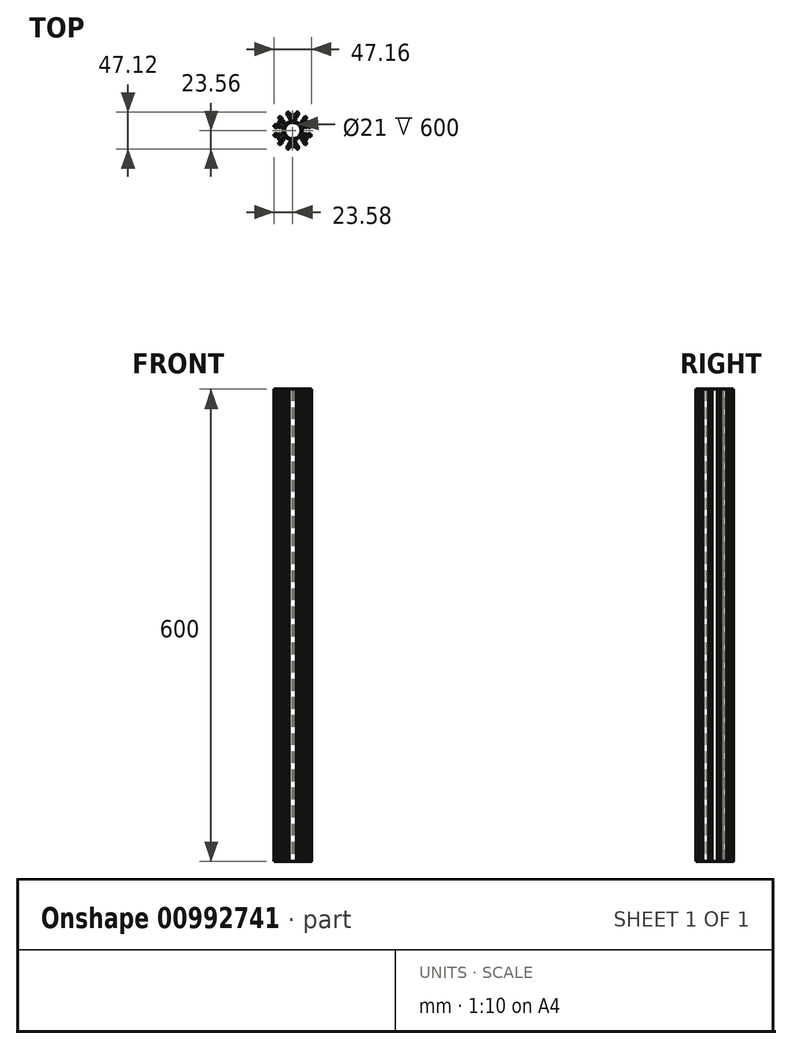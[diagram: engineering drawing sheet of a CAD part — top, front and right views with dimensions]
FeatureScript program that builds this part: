
annotation { "Feature Type Name" : "Feature", "Feature Type Description" : "" }
export const myFeature = defineFeature(function(context is Context, id is Id, definition is map)
    precondition{}
    {
        {
            var Q0;
            Q0=qCreatedBy(makeId("Top.planeOp"),FACE);
            var sketch = newSketch(context, id + "F0", { "sketchPlane" : qUnion([Q0])});
            skLineSegment(sketch, "E0.bottom", {"start": v(-7.45, -23.56) * mm, "end": v(-4.75, -23.56) * mm});
            skLineSegment(sketch, "E0.top", {"start": v(-7.45, -19.16) * mm, "end": v(-1, -19.16) * mm});
            skLineSegment(sketch, "E0.left", {"start": v(-7.45, -23.56) * mm, "end": v(-7.45, -19.16) * mm});
            skLineSegment(sketch, "E0.right", {"start": v(7.45, -23.56) * mm, "end": v(7.45, -19.16) * mm});
            skLineSegment(sketch, "E1.bottom", {"start": v(-6.25, -22.36) * mm, "end": v(-4.75, -22.36) * mm});
            skLineSegment(sketch, "E1.top", {"start": v(-6.25, -20.36) * mm, "end": v(6.25, -20.36) * mm});
            skLineSegment(sketch, "E1.left", {"start": v(-6.25, -22.36) * mm, "end": v(-6.25, -20.36) * mm});
            skLineSegment(sketch, "E1.right", {"start": v(6.25, -22.36) * mm, "end": v(6.25, -20.36) * mm});
            skLineSegment(sketch, "E2.left", {"start": v(-1, -19.16) * mm, "end": v(-1, -17.46) * mm});
            skLineSegment(sketch, "E2.right", {"start": v(1, -19.16) * mm, "end": v(1, -17.46) * mm});
            skArc(sketch, "E3", {"start": v(1, -12.46) * mm, "mid": v(6.25, -10.83) * mm, "end": v(10.3, -7.1) * mm});
            skLineSegment(sketch, "E4.left", {"start": v(-4.75, -23.56) * mm, "end": v(-4.75, -22.36) * mm});
            skLineSegment(sketch, "E4.right", {"start": v(4.75, -23.56) * mm, "end": v(4.75, -22.36) * mm});
            skLineSegment(sketch, "E5.trimOffspring", {"start": v(4.75, -23.56) * mm, "end": v(7.45, -23.56) * mm});
            skLineSegment(sketch, "E6.trimOffspring", {"start": v(4.75, -22.36) * mm, "end": v(6.25, -22.36) * mm});
            skLineSegment(sketch, "E7.trimOffspring", {"start": v(1, -19.16) * mm, "end": v(7.45, -19.16) * mm});
            skCircle(sketch, "E8", {"center": v(0, 0) * mm, "radius": 10.5 * mm});
            skLineSegment(sketch, "E9.bottom", {"start": v(-5.5, -17.46) * mm, "end": v(-1, -17.46) * mm});
            skLineSegment(sketch, "E9.top", {"start": v(-5.5, -16.46) * mm, "end": v(-1, -16.46) * mm});
            skLineSegment(sketch, "E9.left", {"start": v(-5.5, -17.46) * mm, "end": v(-5.5, -16.46) * mm});
            skLineSegment(sketch, "E9.right", {"start": v(5.5, -17.46) * mm, "end": v(5.5, -16.46) * mm});
            skLineSegment(sketch, "E10.bottom", {"start": v(-4, -14.86) * mm, "end": v(-1, -14.86) * mm});
            skLineSegment(sketch, "E10.top", {"start": v(-4, -13.86) * mm, "end": v(-1, -13.86) * mm});
            skLineSegment(sketch, "E10.left", {"start": v(-4, -14.86) * mm, "end": v(-4, -13.86) * mm});
            skLineSegment(sketch, "E10.right", {"start": v(4, -14.86) * mm, "end": v(4, -13.86) * mm});
            skLineSegment(sketch, "E11.trimOffspring", {"start": v(1, -17.46) * mm, "end": v(5.5, -17.46) * mm});
            skLineSegment(sketch, "E12.trimOffspring", {"start": v(-1, -16.46) * mm, "end": v(-1, -14.86) * mm});
            skLineSegment(sketch, "E13.trimOffspring", {"start": v(1, -16.46) * mm, "end": v(5.5, -16.46) * mm});
            skLineSegment(sketch, "E14.trimOffspring", {"start": v(1, -14.86) * mm, "end": v(4, -14.86) * mm});
            skLineSegment(sketch, "E15.trimOffspring", {"start": v(1, -16.46) * mm, "end": v(1, -14.86) * mm});
            skLineSegment(sketch, "E16.trimOffspring", {"start": v(1, -13.86) * mm, "end": v(1, -12.46) * mm});
            skLineSegment(sketch, "E17.trimOffspring", {"start": v(-1, -13.86) * mm, "end": v(-1, -12.46) * mm});
            skLineSegment(sketch, "E18.trimOffspring", {"start": v(1, -13.86) * mm, "end": v(4, -13.86) * mm});
            skLineSegment(sketch, "E19.1.0", {"start": v(16.68, -18.23) * mm, "end": v(18.03, -15.9) * mm});
            skLineSegment(sketch, "E19.1.1", {"start": v(13.37, -6.56) * mm, "end": v(14.87, -3.97) * mm});
            skLineSegment(sketch, "E19.1.2", {"start": v(12.87, -16.03) * mm, "end": v(16.1, -10.45) * mm});
            skLineSegment(sketch, "E19.1.3", {"start": v(24.13, -5.33) * mm, "end": v(20.32, -3.13) * mm});
            skLineSegment(sketch, "E19.1.4", {"start": v(10.87, -10.9) * mm, "end": v(12.37, -8.3) * mm});
            skLineSegment(sketch, "E19.1.5", {"start": v(10, -10.4) * mm, "end": v(11.5, -7.8) * mm});
            skLineSegment(sketch, "E19.1.6", {"start": v(16.24, -16.6) * mm, "end": v(14.5, -15.6) * mm});
            skLineSegment(sketch, "E19.1.7", {"start": v(14.75, -7.36) * mm, "end": v(17, -3.47) * mm});
            skLineSegment(sketch, "E19.1.8", {"start": v(12.5, -6.06) * mm, "end": v(14, -3.47) * mm});
            skLineSegment(sketch, "E19.1.9", {"start": v(22.78, -7.67) * mm, "end": v(24.13, -5.33) * mm});
            skLineSegment(sketch, "E19.1.10", {"start": v(14.5, -15.6) * mm, "end": v(20.76, -4.77) * mm});
            skLineSegment(sketch, "E19.1.11", {"start": v(22.49, -5.77) * mm, "end": v(20.76, -4.77) * mm});
            skLineSegment(sketch, "E19.1.12", {"start": v(16.68, -18.23) * mm, "end": v(12.87, -16.03) * mm});
            skLineSegment(sketch, "E19.1.13", {"start": v(17.1, -8.71) * mm, "end": v(20.32, -3.13) * mm});
            skLineSegment(sketch, "E19.1.14", {"start": v(12.37, -13.5) * mm, "end": v(14.62, -9.6) * mm});
            skLineSegment(sketch, "E19.1.15", {"start": v(11.5, -13) * mm, "end": v(13.75, -9.1) * mm});
            skLineSegment(sketch, "E19.1.16", {"start": v(15.62, -7.86) * mm, "end": v(17.87, -3.97) * mm});
            skLineSegment(sketch, "E19.1.17", {"start": v(22.78, -7.67) * mm, "end": v(21.74, -7.07) * mm});
            skLineSegment(sketch, "E19.1.18", {"start": v(13.75, -9.1) * mm, "end": v(12.37, -8.3) * mm});
            skLineSegment(sketch, "E19.1.19", {"start": v(14.87, -3.97) * mm, "end": v(14, -3.47) * mm});
            skLineSegment(sketch, "E19.1.20", {"start": v(21.74, -7.07) * mm, "end": v(22.49, -5.77) * mm});
            skLineSegment(sketch, "E19.1.21", {"start": v(18.03, -15.9) * mm, "end": v(16.99, -15.3) * mm});
            skLineSegment(sketch, "E19.1.22", {"start": v(10.87, -10.9) * mm, "end": v(10, -10.4) * mm});
            skLineSegment(sketch, "E19.1.23", {"start": v(12.37, -13.5) * mm, "end": v(11.5, -13) * mm});
            skLineSegment(sketch, "E19.1.24", {"start": v(16.1, -10.45) * mm, "end": v(14.62, -9.6) * mm});
            skLineSegment(sketch, "E19.1.25", {"start": v(17.1, -8.71) * mm, "end": v(15.62, -7.86) * mm});
            skLineSegment(sketch, "E19.1.26", {"start": v(16.24, -16.6) * mm, "end": v(16.99, -15.3) * mm});
            skLineSegment(sketch, "E19.1.27", {"start": v(17.87, -3.97) * mm, "end": v(17, -3.47) * mm});
            skLineSegment(sketch, "E19.1.28", {"start": v(14.75, -7.36) * mm, "end": v(13.37, -6.56) * mm});
            skLineSegment(sketch, "E19.1.29", {"start": v(11.5, -7.8) * mm, "end": v(10.3, -7.1) * mm});
            skLineSegment(sketch, "E19.1.30", {"start": v(12.5, -6.06) * mm, "end": v(11.3, -5.36) * mm});
            skLineSegment(sketch, "E19.2.0", {"start": v(24.13, 5.33) * mm, "end": v(22.78, 7.67) * mm});
            skLineSegment(sketch, "E19.2.1", {"start": v(12.37, 8.3) * mm, "end": v(10.87, 10.9) * mm});
            skLineSegment(sketch, "E19.2.2", {"start": v(20.32, 3.13) * mm, "end": v(17.1, 8.71) * mm});
            skLineSegment(sketch, "E19.2.3", {"start": v(16.68, 18.23) * mm, "end": v(12.87, 16.03) * mm});
            skLineSegment(sketch, "E19.2.4", {"start": v(14.87, 3.97) * mm, "end": v(13.37, 6.56) * mm});
            skLineSegment(sketch, "E19.2.5", {"start": v(14, 3.47) * mm, "end": v(12.5, 6.06) * mm});
            skLineSegment(sketch, "E19.2.6", {"start": v(22.49, 5.77) * mm, "end": v(20.76, 4.77) * mm});
            skLineSegment(sketch, "E19.2.7", {"start": v(13.75, 9.1) * mm, "end": v(11.5, 13) * mm});
            skLineSegment(sketch, "E19.2.8", {"start": v(11.5, 7.8) * mm, "end": v(10, 10.4) * mm});
            skLineSegment(sketch, "E19.2.9", {"start": v(18.03, 15.9) * mm, "end": v(16.68, 18.23) * mm});
            skLineSegment(sketch, "E19.2.10", {"start": v(20.76, 4.77) * mm, "end": v(14.5, 15.6) * mm});
            skLineSegment(sketch, "E19.2.11", {"start": v(16.24, 16.6) * mm, "end": v(14.5, 15.6) * mm});
            skLineSegment(sketch, "E19.2.12", {"start": v(24.13, 5.33) * mm, "end": v(20.32, 3.13) * mm});
            skLineSegment(sketch, "E19.2.13", {"start": v(16.1, 10.45) * mm, "end": v(12.87, 16.03) * mm});
            skLineSegment(sketch, "E19.2.14", {"start": v(17.87, 3.97) * mm, "end": v(15.62, 7.86) * mm});
            skLineSegment(sketch, "E19.2.15", {"start": v(17, 3.47) * mm, "end": v(14.75, 7.36) * mm});
            skLineSegment(sketch, "E19.2.16", {"start": v(14.62, 9.6) * mm, "end": v(12.37, 13.5) * mm});
            skLineSegment(sketch, "E19.2.17", {"start": v(18.03, 15.9) * mm, "end": v(16.99, 15.3) * mm});
            skLineSegment(sketch, "E19.2.18", {"start": v(14.75, 7.36) * mm, "end": v(13.37, 6.56) * mm});
            skLineSegment(sketch, "E19.2.19", {"start": v(10.87, 10.9) * mm, "end": v(10, 10.4) * mm});
            skLineSegment(sketch, "E19.2.20", {"start": v(16.99, 15.3) * mm, "end": v(16.24, 16.6) * mm});
            skLineSegment(sketch, "E19.2.21", {"start": v(22.78, 7.67) * mm, "end": v(21.74, 7.07) * mm});
            skLineSegment(sketch, "E19.2.22", {"start": v(14.87, 3.97) * mm, "end": v(14, 3.47) * mm});
            skLineSegment(sketch, "E19.2.23", {"start": v(17.87, 3.97) * mm, "end": v(17, 3.47) * mm});
            skLineSegment(sketch, "E19.2.24", {"start": v(17.1, 8.71) * mm, "end": v(15.62, 7.86) * mm});
            skLineSegment(sketch, "E19.2.25", {"start": v(16.1, 10.45) * mm, "end": v(14.62, 9.6) * mm});
            skLineSegment(sketch, "E19.2.26", {"start": v(22.49, 5.77) * mm, "end": v(21.74, 7.07) * mm});
            skLineSegment(sketch, "E19.2.27", {"start": v(12.37, 13.5) * mm, "end": v(11.5, 13) * mm});
            skLineSegment(sketch, "E19.2.28", {"start": v(13.75, 9.1) * mm, "end": v(12.37, 8.3) * mm});
            skLineSegment(sketch, "E19.2.29", {"start": v(12.5, 6.06) * mm, "end": v(11.3, 5.36) * mm});
            skLineSegment(sketch, "E19.2.30", {"start": v(11.5, 7.8) * mm, "end": v(10.3, 7.1) * mm});
            skLineSegment(sketch, "E19.3.0", {"start": v(7.45, 23.56) * mm, "end": v(4.75, 23.56) * mm});
            skLineSegment(sketch, "E19.3.1", {"start": v(-1, 14.86) * mm, "end": v(-4, 14.86) * mm});
            skLineSegment(sketch, "E19.3.2", {"start": v(7.45, 19.16) * mm, "end": v(1, 19.16) * mm});
            skLineSegment(sketch, "E19.3.3", {"start": v(-7.45, 23.56) * mm, "end": v(-7.45, 19.16) * mm});
            skLineSegment(sketch, "E19.3.4", {"start": v(4, 14.86) * mm, "end": v(1, 14.86) * mm});
            skLineSegment(sketch, "E19.3.5", {"start": v(4, 13.86) * mm, "end": v(1, 13.86) * mm});
            skLineSegment(sketch, "E19.3.6", {"start": v(6.25, 22.36) * mm, "end": v(6.25, 20.36) * mm});
            skLineSegment(sketch, "E19.3.7", {"start": v(-1, 16.46) * mm, "end": v(-5.5, 16.46) * mm});
            skLineSegment(sketch, "E19.3.8", {"start": v(-1, 13.86) * mm, "end": v(-4, 13.86) * mm});
            skLineSegment(sketch, "E19.3.9", {"start": v(-4.75, 23.56) * mm, "end": v(-7.45, 23.56) * mm});
            skLineSegment(sketch, "E19.3.10", {"start": v(6.25, 20.36) * mm, "end": v(-6.25, 20.36) * mm});
            skLineSegment(sketch, "E19.3.11", {"start": v(-6.25, 22.36) * mm, "end": v(-6.25, 20.36) * mm});
            skLineSegment(sketch, "E19.3.12", {"start": v(7.45, 23.56) * mm, "end": v(7.45, 19.16) * mm});
            skLineSegment(sketch, "E19.3.13", {"start": v(-1, 19.16) * mm, "end": v(-7.45, 19.16) * mm});
            skLineSegment(sketch, "E19.3.14", {"start": v(5.5, 17.46) * mm, "end": v(1, 17.46) * mm});
            skLineSegment(sketch, "E19.3.15", {"start": v(5.5, 16.46) * mm, "end": v(1, 16.46) * mm});
            skLineSegment(sketch, "E19.3.16", {"start": v(-1, 17.46) * mm, "end": v(-5.5, 17.46) * mm});
            skLineSegment(sketch, "E19.3.17", {"start": v(-4.75, 23.56) * mm, "end": v(-4.75, 22.36) * mm});
            skLineSegment(sketch, "E19.3.18", {"start": v(1, 16.46) * mm, "end": v(1, 14.86) * mm});
            skLineSegment(sketch, "E19.3.19", {"start": v(-4, 14.86) * mm, "end": v(-4, 13.86) * mm});
            skLineSegment(sketch, "E19.3.20", {"start": v(-4.75, 22.36) * mm, "end": v(-6.25, 22.36) * mm});
            skLineSegment(sketch, "E19.3.21", {"start": v(4.75, 23.56) * mm, "end": v(4.75, 22.36) * mm});
            skLineSegment(sketch, "E19.3.22", {"start": v(4, 14.86) * mm, "end": v(4, 13.86) * mm});
            skLineSegment(sketch, "E19.3.23", {"start": v(5.5, 17.46) * mm, "end": v(5.5, 16.46) * mm});
            skLineSegment(sketch, "E19.3.24", {"start": v(1, 19.16) * mm, "end": v(1, 17.46) * mm});
            skLineSegment(sketch, "E19.3.25", {"start": v(-1, 19.16) * mm, "end": v(-1, 17.46) * mm});
            skLineSegment(sketch, "E19.3.26", {"start": v(6.25, 22.36) * mm, "end": v(4.75, 22.36) * mm});
            skLineSegment(sketch, "E19.3.27", {"start": v(-5.5, 17.46) * mm, "end": v(-5.5, 16.46) * mm});
            skLineSegment(sketch, "E19.3.28", {"start": v(-1, 16.46) * mm, "end": v(-1, 14.86) * mm});
            skLineSegment(sketch, "E19.3.29", {"start": v(1, 13.86) * mm, "end": v(1, 12.46) * mm});
            skLineSegment(sketch, "E19.3.30", {"start": v(-1, 13.86) * mm, "end": v(-1, 12.46) * mm});
            skLineSegment(sketch, "E19.4.0", {"start": v(-16.68, 18.23) * mm, "end": v(-18.03, 15.9) * mm});
            skLineSegment(sketch, "E19.4.1", {"start": v(-13.37, 6.56) * mm, "end": v(-14.87, 3.97) * mm});
            skLineSegment(sketch, "E19.4.2", {"start": v(-12.87, 16.03) * mm, "end": v(-16.1, 10.45) * mm});
            skLineSegment(sketch, "E19.4.3", {"start": v(-24.13, 5.33) * mm, "end": v(-20.32, 3.13) * mm});
            skLineSegment(sketch, "E19.4.4", {"start": v(-10.87, 10.9) * mm, "end": v(-12.37, 8.3) * mm});
            skLineSegment(sketch, "E19.4.5", {"start": v(-10, 10.4) * mm, "end": v(-11.5, 7.8) * mm});
            skLineSegment(sketch, "E19.4.6", {"start": v(-16.24, 16.6) * mm, "end": v(-14.5, 15.6) * mm});
            skLineSegment(sketch, "E19.4.7", {"start": v(-14.75, 7.36) * mm, "end": v(-17, 3.47) * mm});
            skLineSegment(sketch, "E19.4.8", {"start": v(-12.5, 6.06) * mm, "end": v(-14, 3.47) * mm});
            skLineSegment(sketch, "E19.4.9", {"start": v(-22.78, 7.67) * mm, "end": v(-24.13, 5.33) * mm});
            skLineSegment(sketch, "E19.4.10", {"start": v(-14.5, 15.6) * mm, "end": v(-20.76, 4.77) * mm});
            skLineSegment(sketch, "E19.4.11", {"start": v(-22.49, 5.77) * mm, "end": v(-20.76, 4.77) * mm});
            skLineSegment(sketch, "E19.4.12", {"start": v(-16.68, 18.23) * mm, "end": v(-12.87, 16.03) * mm});
            skLineSegment(sketch, "E19.4.13", {"start": v(-17.1, 8.71) * mm, "end": v(-20.32, 3.13) * mm});
            skLineSegment(sketch, "E19.4.14", {"start": v(-12.37, 13.5) * mm, "end": v(-14.62, 9.6) * mm});
            skLineSegment(sketch, "E19.4.15", {"start": v(-11.5, 13) * mm, "end": v(-13.75, 9.1) * mm});
            skLineSegment(sketch, "E19.4.16", {"start": v(-15.62, 7.86) * mm, "end": v(-17.87, 3.97) * mm});
            skLineSegment(sketch, "E19.4.17", {"start": v(-22.78, 7.67) * mm, "end": v(-21.74, 7.07) * mm});
            skLineSegment(sketch, "E19.4.18", {"start": v(-13.75, 9.1) * mm, "end": v(-12.37, 8.3) * mm});
            skLineSegment(sketch, "E19.4.19", {"start": v(-14.87, 3.97) * mm, "end": v(-14, 3.47) * mm});
            skLineSegment(sketch, "E19.4.20", {"start": v(-21.74, 7.07) * mm, "end": v(-22.49, 5.77) * mm});
            skLineSegment(sketch, "E19.4.21", {"start": v(-18.03, 15.9) * mm, "end": v(-16.99, 15.3) * mm});
            skLineSegment(sketch, "E19.4.22", {"start": v(-10.87, 10.9) * mm, "end": v(-10, 10.4) * mm});
            skLineSegment(sketch, "E19.4.23", {"start": v(-12.37, 13.5) * mm, "end": v(-11.5, 13) * mm});
            skLineSegment(sketch, "E19.4.24", {"start": v(-16.1, 10.45) * mm, "end": v(-14.62, 9.6) * mm});
            skLineSegment(sketch, "E19.4.25", {"start": v(-17.1, 8.71) * mm, "end": v(-15.62, 7.86) * mm});
            skLineSegment(sketch, "E19.4.26", {"start": v(-16.24, 16.6) * mm, "end": v(-16.99, 15.3) * mm});
            skLineSegment(sketch, "E19.4.27", {"start": v(-17.87, 3.97) * mm, "end": v(-17, 3.47) * mm});
            skLineSegment(sketch, "E19.4.28", {"start": v(-14.75, 7.36) * mm, "end": v(-13.37, 6.56) * mm});
            skLineSegment(sketch, "E19.4.29", {"start": v(-11.5, 7.8) * mm, "end": v(-10.3, 7.1) * mm});
            skLineSegment(sketch, "E19.4.30", {"start": v(-12.5, 6.06) * mm, "end": v(-11.3, 5.36) * mm});
            skLineSegment(sketch, "E19.5.0", {"start": v(-24.13, -5.33) * mm, "end": v(-22.78, -7.67) * mm});
            skLineSegment(sketch, "E19.5.1", {"start": v(-12.37, -8.3) * mm, "end": v(-10.87, -10.9) * mm});
            skLineSegment(sketch, "E19.5.2", {"start": v(-20.32, -3.13) * mm, "end": v(-17.1, -8.71) * mm});
            skLineSegment(sketch, "E19.5.3", {"start": v(-16.68, -18.23) * mm, "end": v(-12.87, -16.03) * mm});
            skLineSegment(sketch, "E19.5.4", {"start": v(-14.87, -3.97) * mm, "end": v(-13.37, -6.56) * mm});
            skLineSegment(sketch, "E19.5.5", {"start": v(-14, -3.47) * mm, "end": v(-12.5, -6.06) * mm});
            skLineSegment(sketch, "E19.5.6", {"start": v(-22.49, -5.77) * mm, "end": v(-20.76, -4.77) * mm});
            skLineSegment(sketch, "E19.5.7", {"start": v(-13.75, -9.1) * mm, "end": v(-11.5, -13) * mm});
            skLineSegment(sketch, "E19.5.8", {"start": v(-11.5, -7.8) * mm, "end": v(-10, -10.4) * mm});
            skLineSegment(sketch, "E19.5.9", {"start": v(-18.03, -15.9) * mm, "end": v(-16.68, -18.23) * mm});
            skLineSegment(sketch, "E19.5.10", {"start": v(-20.76, -4.77) * mm, "end": v(-14.5, -15.6) * mm});
            skLineSegment(sketch, "E19.5.11", {"start": v(-16.24, -16.6) * mm, "end": v(-14.5, -15.6) * mm});
            skLineSegment(sketch, "E19.5.12", {"start": v(-24.13, -5.33) * mm, "end": v(-20.32, -3.13) * mm});
            skLineSegment(sketch, "E19.5.13", {"start": v(-16.1, -10.45) * mm, "end": v(-12.87, -16.03) * mm});
            skLineSegment(sketch, "E19.5.14", {"start": v(-17.87, -3.97) * mm, "end": v(-15.62, -7.86) * mm});
            skLineSegment(sketch, "E19.5.15", {"start": v(-17, -3.47) * mm, "end": v(-14.75, -7.36) * mm});
            skLineSegment(sketch, "E19.5.16", {"start": v(-14.62, -9.6) * mm, "end": v(-12.37, -13.5) * mm});
            skLineSegment(sketch, "E19.5.17", {"start": v(-18.03, -15.9) * mm, "end": v(-16.99, -15.3) * mm});
            skLineSegment(sketch, "E19.5.18", {"start": v(-14.75, -7.36) * mm, "end": v(-13.37, -6.56) * mm});
            skLineSegment(sketch, "E19.5.19", {"start": v(-10.87, -10.9) * mm, "end": v(-10, -10.4) * mm});
            skLineSegment(sketch, "E19.5.20", {"start": v(-16.99, -15.3) * mm, "end": v(-16.24, -16.6) * mm});
            skLineSegment(sketch, "E19.5.21", {"start": v(-22.78, -7.67) * mm, "end": v(-21.74, -7.07) * mm});
            skLineSegment(sketch, "E19.5.22", {"start": v(-14.87, -3.97) * mm, "end": v(-14, -3.47) * mm});
            skLineSegment(sketch, "E19.5.23", {"start": v(-17.87, -3.97) * mm, "end": v(-17, -3.47) * mm});
            skLineSegment(sketch, "E19.5.24", {"start": v(-17.1, -8.71) * mm, "end": v(-15.62, -7.86) * mm});
            skLineSegment(sketch, "E19.5.25", {"start": v(-16.1, -10.45) * mm, "end": v(-14.62, -9.6) * mm});
            skLineSegment(sketch, "E19.5.26", {"start": v(-22.49, -5.77) * mm, "end": v(-21.74, -7.07) * mm});
            skLineSegment(sketch, "E19.5.27", {"start": v(-12.37, -13.5) * mm, "end": v(-11.5, -13) * mm});
            skLineSegment(sketch, "E19.5.28", {"start": v(-13.75, -9.1) * mm, "end": v(-12.37, -8.3) * mm});
            skLineSegment(sketch, "E19.5.29", {"start": v(-12.5, -6.06) * mm, "end": v(-11.3, -5.36) * mm});
            skLineSegment(sketch, "E19.5.30", {"start": v(-11.5, -7.8) * mm, "end": v(-10.3, -7.1) * mm});
            skArc(sketch, "E20.trimOffspring", {"start": v(-10.3, -7.1) * mm, "mid": v(-6.25, -10.83) * mm, "end": v(-1, -12.46) * mm});
            skArc(sketch, "E21.trimOffspring", {"start": v(-11.3, 5.36) * mm, "mid": v(-12.5, 0) * mm, "end": v(-11.3, -5.36) * mm});
            skArc(sketch, "E22.trimOffspring", {"start": v(11.3, -5.36) * mm, "mid": v(12.5, 0) * mm, "end": v(11.3, 5.36) * mm});
            skArc(sketch, "E23.trimOffspring", {"start": v(-1, 12.46) * mm, "mid": v(-6.25, 10.83) * mm, "end": v(-10.3, 7.1) * mm});
            skArc(sketch, "E24.trimOffspring", {"start": v(10.3, 7.1) * mm, "mid": v(6.25, 10.83) * mm, "end": v(1, 12.46) * mm});
            skSolve(sketch);
        }
        {
            var Q0;
            Q0=qSketchRegion(id+"F0",true);
            extrude(context, id + "F1", {"entities" : qUnion([Q0]), "depth" : 600 * mm, "offsetDistance" : 25 * mm});
        }
        {
            var Q0;
            Q0=makeQuery(id+"F1.opExtrude","SWEPT_EDGE",EDGE,{"disambiguationData":[OSD([sQuery(id+"F0.wireOp",EDGE,"E19.3.2"),sQuery(id+"F0.wireOp",EDGE,"E19.3.12")])]});
            var Q1;
            Q1=makeQuery(id+"F1.opExtrude","SWEPT_EDGE",EDGE,{"disambiguationData":[OSD([sQuery(id+"F0.wireOp",EDGE,"E19.3.3"),sQuery(id+"F0.wireOp",EDGE,"E19.3.13")])]});
            var Q2;
            Q2=makeQuery(id+"F1.opExtrude","SWEPT_EDGE",EDGE,{"disambiguationData":[OSD([sQuery(id+"F0.wireOp",EDGE,"E19.2.3"),sQuery(id+"F0.wireOp",EDGE,"E19.2.13")])]});
            var Q3;
            Q3=makeQuery(id+"F1.opExtrude","SWEPT_EDGE",EDGE,{"disambiguationData":[OSD([sQuery(id+"F0.wireOp",EDGE,"E19.2.2"),sQuery(id+"F0.wireOp",EDGE,"E19.2.12")])]});
            var Q4;
            Q4=makeQuery(id+"F1.opExtrude","SWEPT_EDGE",EDGE,{"disambiguationData":[OSD([sQuery(id+"F0.wireOp",EDGE,"E19.1.3"),sQuery(id+"F0.wireOp",EDGE,"E19.1.13")])]});
            var Q5;
            Q5=makeQuery(id+"F1.opExtrude","SWEPT_EDGE",EDGE,{"disambiguationData":[OSD([sQuery(id+"F0.wireOp",EDGE,"E19.1.2"),sQuery(id+"F0.wireOp",EDGE,"E19.1.12")])]});
            var Q6;
            Q6=makeQuery(id+"F1.opExtrude","SWEPT_EDGE",EDGE,{"disambiguationData":[OSD([sQuery(id+"F0.wireOp",EDGE,"E0.right"),sQuery(id+"F0.wireOp",EDGE,"E7.trimOffspring")])]});
            var Q7;
            Q7=makeQuery(id+"F1.opExtrude","SWEPT_EDGE",EDGE,{"disambiguationData":[OSD([sQuery(id+"F0.wireOp",EDGE,"E0.top"),sQuery(id+"F0.wireOp",EDGE,"E0.left")])]});
            var Q8;
            Q8=makeQuery(id+"F1.opExtrude","SWEPT_EDGE",EDGE,{"disambiguationData":[OSD([sQuery(id+"F0.wireOp",EDGE,"E19.5.3"),sQuery(id+"F0.wireOp",EDGE,"E19.5.13")])]});
            var Q9;
            Q9=makeQuery(id+"F1.opExtrude","SWEPT_EDGE",EDGE,{"disambiguationData":[OSD([sQuery(id+"F0.wireOp",EDGE,"E19.5.2"),sQuery(id+"F0.wireOp",EDGE,"E19.5.12")])]});
            var Q10;
            Q10=makeQuery(id+"F1.opExtrude","SWEPT_EDGE",EDGE,{"disambiguationData":[OSD([sQuery(id+"F0.wireOp",EDGE,"E19.4.3"),sQuery(id+"F0.wireOp",EDGE,"E19.4.13")])]});
            var Q11;
            Q11=makeQuery(id+"F1.opExtrude","SWEPT_EDGE",EDGE,{"disambiguationData":[OSD([sQuery(id+"F0.wireOp",EDGE,"E19.4.2"),sQuery(id+"F0.wireOp",EDGE,"E19.4.12")])]});
            fillet(context, id + "F2", {"entities" : qUnion([Q0, Q1, Q2, Q3, Q4, Q5, Q6, Q7, Q8, Q9, Q10, Q11]), "tangentPropagation" : true, "radius" : 1.5 * mm, "defaultsChanged" : true, "vertexSettings" : [], "allowEdgeOverflow" : false});
        }
        {
            var Q0;
            Q0=makeQuery(id+"F1.opExtrude","SWEPT_EDGE",EDGE,{"disambiguationData":[OSD([sQuery(id+"F0.wireOp",EDGE,"E19.3.0"),sQuery(id+"F0.wireOp",EDGE,"E19.3.21")])]});
            var Q1;
            Q1=makeQuery(id+"F1.opExtrude","SWEPT_EDGE",EDGE,{"disambiguationData":[OSD([sQuery(id+"F0.wireOp",EDGE,"E19.3.9"),sQuery(id+"F0.wireOp",EDGE,"E19.3.17")])]});
            var Q2;
            Q2=makeQuery(id+"F1.opExtrude","SWEPT_EDGE",EDGE,{"disambiguationData":[OSD([sQuery(id+"F0.wireOp",EDGE,"E19.3.16"),sQuery(id+"F0.wireOp",EDGE,"E19.3.27")])]});
            var Q3;
            Q3=makeQuery(id+"F1.opExtrude","SWEPT_EDGE",EDGE,{"disambiguationData":[OSD([sQuery(id+"F0.wireOp",EDGE,"E19.3.7"),sQuery(id+"F0.wireOp",EDGE,"E19.3.27")])]});
            var Q4;
            Q4=makeQuery(id+"F1.opExtrude","SWEPT_EDGE",EDGE,{"disambiguationData":[OSD([sQuery(id+"F0.wireOp",EDGE,"E19.3.1"),sQuery(id+"F0.wireOp",EDGE,"E19.3.19")])]});
            var Q5;
            Q5=makeQuery(id+"F1.opExtrude","SWEPT_EDGE",EDGE,{"disambiguationData":[OSD([sQuery(id+"F0.wireOp",EDGE,"E19.3.8"),sQuery(id+"F0.wireOp",EDGE,"E19.3.19")])]});
            var Q6;
            Q6=makeQuery(id+"F1.opExtrude","SWEPT_EDGE",EDGE,{"disambiguationData":[OSD([sQuery(id+"F0.wireOp",EDGE,"E19.3.14"),sQuery(id+"F0.wireOp",EDGE,"E19.3.23")])]});
            var Q7;
            Q7=makeQuery(id+"F1.opExtrude","SWEPT_EDGE",EDGE,{"disambiguationData":[OSD([sQuery(id+"F0.wireOp",EDGE,"E19.3.15"),sQuery(id+"F0.wireOp",EDGE,"E19.3.23")])]});
            var Q8;
            Q8=makeQuery(id+"F1.opExtrude","SWEPT_EDGE",EDGE,{"disambiguationData":[OSD([sQuery(id+"F0.wireOp",EDGE,"E19.3.4"),sQuery(id+"F0.wireOp",EDGE,"E19.3.22")])]});
            var Q9;
            Q9=makeQuery(id+"F1.opExtrude","SWEPT_EDGE",EDGE,{"disambiguationData":[OSD([sQuery(id+"F0.wireOp",EDGE,"E19.3.5"),sQuery(id+"F0.wireOp",EDGE,"E19.3.22")])]});
            var Q10;
            Q10=makeQuery(id+"F1.opExtrude","SWEPT_EDGE",EDGE,{"disambiguationData":[OSD([sQuery(id+"F0.wireOp",EDGE,"E19.4.0"),sQuery(id+"F0.wireOp",EDGE,"E19.4.21")])]});
            var Q11;
            Q11=makeQuery(id+"F1.opExtrude","SWEPT_EDGE",EDGE,{"disambiguationData":[OSD([sQuery(id+"F0.wireOp",EDGE,"E19.4.9"),sQuery(id+"F0.wireOp",EDGE,"E19.4.17")])]});
            var Q12;
            Q12=makeQuery(id+"F1.opExtrude","SWEPT_EDGE",EDGE,{"disambiguationData":[OSD([sQuery(id+"F0.wireOp",EDGE,"E19.4.16"),sQuery(id+"F0.wireOp",EDGE,"E19.4.27")])]});
            var Q13;
            Q13=makeQuery(id+"F1.opExtrude","SWEPT_EDGE",EDGE,{"disambiguationData":[OSD([sQuery(id+"F0.wireOp",EDGE,"E19.4.7"),sQuery(id+"F0.wireOp",EDGE,"E19.4.27")])]});
            var Q14;
            Q14=makeQuery(id+"F1.opExtrude","SWEPT_EDGE",EDGE,{"disambiguationData":[OSD([sQuery(id+"F0.wireOp",EDGE,"E19.4.1"),sQuery(id+"F0.wireOp",EDGE,"E19.4.19")])]});
            var Q15;
            Q15=makeQuery(id+"F1.opExtrude","SWEPT_EDGE",EDGE,{"disambiguationData":[OSD([sQuery(id+"F0.wireOp",EDGE,"E19.4.8"),sQuery(id+"F0.wireOp",EDGE,"E19.4.19")])]});
            var Q16;
            Q16=makeQuery(id+"F1.opExtrude","SWEPT_EDGE",EDGE,{"disambiguationData":[OSD([sQuery(id+"F0.wireOp",EDGE,"E19.4.4"),sQuery(id+"F0.wireOp",EDGE,"E19.4.22")])]});
            var Q17;
            Q17=makeQuery(id+"F1.opExtrude","SWEPT_EDGE",EDGE,{"disambiguationData":[OSD([sQuery(id+"F0.wireOp",EDGE,"E19.4.14"),sQuery(id+"F0.wireOp",EDGE,"E19.4.23")])]});
            var Q18;
            Q18=makeQuery(id+"F1.opExtrude","SWEPT_EDGE",EDGE,{"disambiguationData":[OSD([sQuery(id+"F0.wireOp",EDGE,"E19.4.15"),sQuery(id+"F0.wireOp",EDGE,"E19.4.23")])]});
            var Q19;
            Q19=makeQuery(id+"F1.opExtrude","SWEPT_EDGE",EDGE,{"disambiguationData":[OSD([sQuery(id+"F0.wireOp",EDGE,"E19.4.5"),sQuery(id+"F0.wireOp",EDGE,"E19.4.22")])]});
            var Q20;
            Q20=makeQuery(id+"F1.opExtrude","SWEPT_EDGE",EDGE,{"disambiguationData":[OSD([sQuery(id+"F0.wireOp",EDGE,"E19.5.0"),sQuery(id+"F0.wireOp",EDGE,"E19.5.21")])]});
            var Q21;
            Q21=makeQuery(id+"F1.opExtrude","SWEPT_EDGE",EDGE,{"disambiguationData":[OSD([sQuery(id+"F0.wireOp",EDGE,"E19.5.14"),sQuery(id+"F0.wireOp",EDGE,"E19.5.23")])]});
            var Q22;
            Q22=makeQuery(id+"F1.opExtrude","SWEPT_EDGE",EDGE,{"disambiguationData":[OSD([sQuery(id+"F0.wireOp",EDGE,"E19.5.15"),sQuery(id+"F0.wireOp",EDGE,"E19.5.23")])]});
            var Q23;
            Q23=makeQuery(id+"F1.opExtrude","SWEPT_EDGE",EDGE,{"disambiguationData":[OSD([sQuery(id+"F0.wireOp",EDGE,"E19.5.4"),sQuery(id+"F0.wireOp",EDGE,"E19.5.22")])]});
            var Q24;
            Q24=makeQuery(id+"F1.opExtrude","SWEPT_EDGE",EDGE,{"disambiguationData":[OSD([sQuery(id+"F0.wireOp",EDGE,"E19.5.5"),sQuery(id+"F0.wireOp",EDGE,"E19.5.22")])]});
            var Q25;
            Q25=makeQuery(id+"F1.opExtrude","SWEPT_EDGE",EDGE,{"disambiguationData":[OSD([sQuery(id+"F0.wireOp",EDGE,"E19.5.1"),sQuery(id+"F0.wireOp",EDGE,"E19.5.19")])]});
            var Q26;
            Q26=makeQuery(id+"F1.opExtrude","SWEPT_EDGE",EDGE,{"disambiguationData":[OSD([sQuery(id+"F0.wireOp",EDGE,"E19.5.8"),sQuery(id+"F0.wireOp",EDGE,"E19.5.19")])]});
            var Q27;
            Q27=makeQuery(id+"F1.opExtrude","SWEPT_EDGE",EDGE,{"disambiguationData":[OSD([sQuery(id+"F0.wireOp",EDGE,"E19.5.7"),sQuery(id+"F0.wireOp",EDGE,"E19.5.27")])]});
            var Q28;
            Q28=makeQuery(id+"F1.opExtrude","SWEPT_EDGE",EDGE,{"disambiguationData":[OSD([sQuery(id+"F0.wireOp",EDGE,"E19.5.16"),sQuery(id+"F0.wireOp",EDGE,"E19.5.27")])]});
            var Q29;
            Q29=makeQuery(id+"F1.opExtrude","SWEPT_EDGE",EDGE,{"disambiguationData":[OSD([sQuery(id+"F0.wireOp",EDGE,"E19.5.9"),sQuery(id+"F0.wireOp",EDGE,"E19.5.17")])]});
            var Q30;
            Q30=makeQuery(id+"F1.opExtrude","SWEPT_EDGE",EDGE,{"disambiguationData":[OSD([sQuery(id+"F0.wireOp",EDGE,"E9.bottom"),sQuery(id+"F0.wireOp",EDGE,"E9.left")])]});
            var Q31;
            Q31=makeQuery(id+"F1.opExtrude","SWEPT_EDGE",EDGE,{"disambiguationData":[OSD([sQuery(id+"F0.wireOp",EDGE,"E9.top"),sQuery(id+"F0.wireOp",EDGE,"E9.left")])]});
            var Q32;
            Q32=makeQuery(id+"F1.opExtrude","SWEPT_EDGE",EDGE,{"disambiguationData":[OSD([sQuery(id+"F0.wireOp",EDGE,"E10.bottom"),sQuery(id+"F0.wireOp",EDGE,"E10.left")])]});
            var Q33;
            Q33=makeQuery(id+"F1.opExtrude","SWEPT_EDGE",EDGE,{"disambiguationData":[OSD([sQuery(id+"F0.wireOp",EDGE,"E10.top"),sQuery(id+"F0.wireOp",EDGE,"E10.left")])]});
            var Q34;
            Q34=makeQuery(id+"F1.opExtrude","SWEPT_EDGE",EDGE,{"disambiguationData":[OSD([sQuery(id+"F0.wireOp",EDGE,"E0.bottom"),sQuery(id+"F0.wireOp",EDGE,"E4.left")])]});
            var Q35;
            Q35=makeQuery(id+"F1.opExtrude","SWEPT_EDGE",EDGE,{"disambiguationData":[OSD([sQuery(id+"F0.wireOp",EDGE,"E4.right"),sQuery(id+"F0.wireOp",EDGE,"E5.trimOffspring")])]});
            var Q36;
            Q36=makeQuery(id+"F1.opExtrude","SWEPT_EDGE",EDGE,{"disambiguationData":[OSD([sQuery(id+"F0.wireOp",EDGE,"E9.right"),sQuery(id+"F0.wireOp",EDGE,"E11.trimOffspring")])]});
            var Q37;
            Q37=makeQuery(id+"F1.opExtrude","SWEPT_EDGE",EDGE,{"disambiguationData":[OSD([sQuery(id+"F0.wireOp",EDGE,"E9.right"),sQuery(id+"F0.wireOp",EDGE,"E13.trimOffspring")])]});
            var Q38;
            Q38=makeQuery(id+"F1.opExtrude","SWEPT_EDGE",EDGE,{"disambiguationData":[OSD([sQuery(id+"F0.wireOp",EDGE,"E10.right"),sQuery(id+"F0.wireOp",EDGE,"E14.trimOffspring")])]});
            var Q39;
            Q39=makeQuery(id+"F1.opExtrude","SWEPT_EDGE",EDGE,{"disambiguationData":[OSD([sQuery(id+"F0.wireOp",EDGE,"E10.right"),sQuery(id+"F0.wireOp",EDGE,"E18.trimOffspring")])]});
            var Q40;
            Q40=makeQuery(id+"F1.opExtrude","SWEPT_EDGE",EDGE,{"disambiguationData":[OSD([sQuery(id+"F0.wireOp",EDGE,"E19.1.14"),sQuery(id+"F0.wireOp",EDGE,"E19.1.23")])]});
            var Q41;
            Q41=makeQuery(id+"F1.opExtrude","SWEPT_EDGE",EDGE,{"disambiguationData":[OSD([sQuery(id+"F0.wireOp",EDGE,"E19.1.15"),sQuery(id+"F0.wireOp",EDGE,"E19.1.23")])]});
            var Q42;
            Q42=makeQuery(id+"F1.opExtrude","SWEPT_EDGE",EDGE,{"disambiguationData":[OSD([sQuery(id+"F0.wireOp",EDGE,"E19.1.5"),sQuery(id+"F0.wireOp",EDGE,"E19.1.22")])]});
            var Q43;
            Q43=makeQuery(id+"F1.opExtrude","SWEPT_EDGE",EDGE,{"disambiguationData":[OSD([sQuery(id+"F0.wireOp",EDGE,"E19.1.4"),sQuery(id+"F0.wireOp",EDGE,"E19.1.22")])]});
            var Q44;
            Q44=makeQuery(id+"F1.opExtrude","SWEPT_EDGE",EDGE,{"disambiguationData":[OSD([sQuery(id+"F0.wireOp",EDGE,"E19.1.0"),sQuery(id+"F0.wireOp",EDGE,"E19.1.21")])]});
            var Q45;
            Q45=makeQuery(id+"F1.opExtrude","SWEPT_EDGE",EDGE,{"disambiguationData":[OSD([sQuery(id+"F0.wireOp",EDGE,"E19.1.9"),sQuery(id+"F0.wireOp",EDGE,"E19.1.17")])]});
            var Q46;
            Q46=makeQuery(id+"F1.opExtrude","SWEPT_EDGE",EDGE,{"disambiguationData":[OSD([sQuery(id+"F0.wireOp",EDGE,"E19.1.16"),sQuery(id+"F0.wireOp",EDGE,"E19.1.27")])]});
            var Q47;
            Q47=makeQuery(id+"F1.opExtrude","SWEPT_EDGE",EDGE,{"disambiguationData":[OSD([sQuery(id+"F0.wireOp",EDGE,"E19.1.1"),sQuery(id+"F0.wireOp",EDGE,"E19.1.19")])]});
            var Q48;
            Q48=makeQuery(id+"F1.opExtrude","SWEPT_EDGE",EDGE,{"disambiguationData":[OSD([sQuery(id+"F0.wireOp",EDGE,"E19.1.7"),sQuery(id+"F0.wireOp",EDGE,"E19.1.27")])]});
            var Q49;
            Q49=makeQuery(id+"F1.opExtrude","SWEPT_EDGE",EDGE,{"disambiguationData":[OSD([sQuery(id+"F0.wireOp",EDGE,"E19.1.8"),sQuery(id+"F0.wireOp",EDGE,"E19.1.19")])]});
            var Q50;
            Q50=makeQuery(id+"F1.opExtrude","SWEPT_EDGE",EDGE,{"disambiguationData":[OSD([sQuery(id+"F0.wireOp",EDGE,"E19.2.15"),sQuery(id+"F0.wireOp",EDGE,"E19.2.23")])]});
            var Q51;
            Q51=makeQuery(id+"F1.opExtrude","SWEPT_EDGE",EDGE,{"disambiguationData":[OSD([sQuery(id+"F0.wireOp",EDGE,"E19.2.14"),sQuery(id+"F0.wireOp",EDGE,"E19.2.23")])]});
            var Q52;
            Q52=makeQuery(id+"F1.opExtrude","SWEPT_EDGE",EDGE,{"disambiguationData":[OSD([sQuery(id+"F0.wireOp",EDGE,"E19.2.4"),sQuery(id+"F0.wireOp",EDGE,"E19.2.22")])]});
            var Q53;
            Q53=makeQuery(id+"F1.opExtrude","SWEPT_EDGE",EDGE,{"disambiguationData":[OSD([sQuery(id+"F0.wireOp",EDGE,"E19.2.5"),sQuery(id+"F0.wireOp",EDGE,"E19.2.22")])]});
            var Q54;
            Q54=makeQuery(id+"F1.opExtrude","SWEPT_EDGE",EDGE,{"disambiguationData":[OSD([sQuery(id+"F0.wireOp",EDGE,"E19.2.8"),sQuery(id+"F0.wireOp",EDGE,"E19.2.19")])]});
            var Q55;
            Q55=makeQuery(id+"F1.opExtrude","SWEPT_EDGE",EDGE,{"disambiguationData":[OSD([sQuery(id+"F0.wireOp",EDGE,"E19.2.7"),sQuery(id+"F0.wireOp",EDGE,"E19.2.27")])]});
            var Q56;
            Q56=makeQuery(id+"F1.opExtrude","SWEPT_EDGE",EDGE,{"disambiguationData":[OSD([sQuery(id+"F0.wireOp",EDGE,"E19.2.9"),sQuery(id+"F0.wireOp",EDGE,"E19.2.17")])]});
            var Q57;
            Q57=makeQuery(id+"F1.opExtrude","SWEPT_EDGE",EDGE,{"disambiguationData":[OSD([sQuery(id+"F0.wireOp",EDGE,"E19.2.0"),sQuery(id+"F0.wireOp",EDGE,"E19.2.21")])]});
            var Q58;
            Q58=makeQuery(id+"F1.opExtrude","SWEPT_EDGE",EDGE,{"disambiguationData":[OSD([sQuery(id+"F0.wireOp",EDGE,"E19.2.16"),sQuery(id+"F0.wireOp",EDGE,"E19.2.27")])]});
            var Q59;
            Q59=makeQuery(id+"F1.opExtrude","SWEPT_EDGE",EDGE,{"disambiguationData":[OSD([sQuery(id+"F0.wireOp",EDGE,"E19.2.1"),sQuery(id+"F0.wireOp",EDGE,"E19.2.19")])]});
            fillet(context, id + "F3", {"entities" : qUnion([Q0, Q1, Q2, Q3, Q4, Q5, Q6, Q7, Q8, Q9, Q10, Q11, Q12, Q13, Q14, Q15, Q16, Q17, Q18, Q19, Q20, Q21, Q22, Q23, Q24, Q25, Q26, Q27, Q28, Q29, Q30, Q31, Q32, Q33, Q34, Q35, Q36, Q37, Q38, Q39, Q40, Q41, Q42, Q43, Q44, Q45, Q46, Q47, Q48, Q49, Q50, Q51, Q52, Q53, Q54, Q55, Q56, Q57, Q58, Q59]), "tangentPropagation" : true, "radius" : .5 * mm, "defaultsChanged" : false, "vertexSettings" : [], "allowEdgeOverflow" : false});
        }
        {
            var Q0;
            Q0=makeQuery(id+"F1.opExtrude","SWEPT_EDGE",EDGE,{"disambiguationData":[OSD([sQuery(id+"F0.wireOp",EDGE,"E19.1.2"),sQuery(id+"F0.wireOp",EDGE,"E19.1.24")])]});
            var Q1;
            Q1=makeQuery(id+"F1.opExtrude","SWEPT_EDGE",EDGE,{"disambiguationData":[OSD([sQuery(id+"F0.wireOp",EDGE,"E19.1.13"),sQuery(id+"F0.wireOp",EDGE,"E19.1.25")])]});
            var Q2;
            Q2=makeQuery(id+"F1.opExtrude","SWEPT_EDGE",EDGE,{"disambiguationData":[OSD([sQuery(id+"F0.wireOp",EDGE,"E0.top"),sQuery(id+"F0.wireOp",EDGE,"E2.left")])]});
            var Q3;
            Q3=makeQuery(id+"F1.opExtrude","SWEPT_EDGE",EDGE,{"disambiguationData":[OSD([sQuery(id+"F0.wireOp",EDGE,"E2.right"),sQuery(id+"F0.wireOp",EDGE,"E7.trimOffspring")])]});
            var Q4;
            Q4=makeQuery(id+"F1.opExtrude","SWEPT_EDGE",EDGE,{"disambiguationData":[OSD([sQuery(id+"F0.wireOp",EDGE,"E19.5.13"),sQuery(id+"F0.wireOp",EDGE,"E19.5.25")])]});
            var Q5;
            Q5=makeQuery(id+"F1.opExtrude","SWEPT_EDGE",EDGE,{"disambiguationData":[OSD([sQuery(id+"F0.wireOp",EDGE,"E19.5.2"),sQuery(id+"F0.wireOp",EDGE,"E19.5.24")])]});
            var Q6;
            Q6=makeQuery(id+"F1.opExtrude","SWEPT_EDGE",EDGE,{"disambiguationData":[OSD([sQuery(id+"F0.wireOp",EDGE,"E19.4.13"),sQuery(id+"F0.wireOp",EDGE,"E19.4.25")])]});
            var Q7;
            Q7=makeQuery(id+"F1.opExtrude","SWEPT_EDGE",EDGE,{"disambiguationData":[OSD([sQuery(id+"F0.wireOp",EDGE,"E19.4.2"),sQuery(id+"F0.wireOp",EDGE,"E19.4.24")])]});
            var Q8;
            Q8=makeQuery(id+"F1.opExtrude","SWEPT_EDGE",EDGE,{"disambiguationData":[OSD([sQuery(id+"F0.wireOp",EDGE,"E19.3.13"),sQuery(id+"F0.wireOp",EDGE,"E19.3.25")])]});
            var Q9;
            Q9=makeQuery(id+"F1.opExtrude","SWEPT_EDGE",EDGE,{"disambiguationData":[OSD([sQuery(id+"F0.wireOp",EDGE,"E19.3.2"),sQuery(id+"F0.wireOp",EDGE,"E19.3.24")])]});
            var Q10;
            Q10=makeQuery(id+"F1.opExtrude","SWEPT_EDGE",EDGE,{"disambiguationData":[OSD([sQuery(id+"F0.wireOp",EDGE,"E19.2.13"),sQuery(id+"F0.wireOp",EDGE,"E19.2.25")])]});
            var Q11;
            Q11=makeQuery(id+"F1.opExtrude","SWEPT_EDGE",EDGE,{"disambiguationData":[OSD([sQuery(id+"F0.wireOp",EDGE,"E19.2.2"),sQuery(id+"F0.wireOp",EDGE,"E19.2.24")])]});
            fillet(context, id + "F4", {"entities" : qUnion([Q0, Q1, Q2, Q3, Q4, Q5, Q6, Q7, Q8, Q9, Q10, Q11]), "tangentPropagation" : true, "radius" : .5 * mm, "defaultsChanged" : false, "vertexSettings" : [], "allowEdgeOverflow" : false});
        }
        {
            var Q0;
            Q0=makeQuery(id+"F1.opExtrude","CAP_FACE",FACE,{"disambiguationData":[OSD([sQuery(id+"F0.wireOp",EDGE,"E0.bottom"),sQuery(id+"F0.wireOp",EDGE,"E0.top"),sQuery(id+"F0.wireOp",EDGE,"E0.left"),sQuery(id+"F0.wireOp",EDGE,"E0.right"),sQuery(id+"F0.wireOp",EDGE,"E1.bottom"),sQuery(id+"F0.wireOp",EDGE,"E1.top"),sQuery(id+"F0.wireOp",EDGE,"E1.left"),sQuery(id+"F0.wireOp",EDGE,"E1.right"),sQuery(id+"F0.wireOp",EDGE,"E2.left"),sQuery(id+"F0.wireOp",EDGE,"E2.right"),sQuery(id+"F0.wireOp",EDGE,"E3"),sQuery(id+"F0.wireOp",EDGE,"E4.left"),sQuery(id+"F0.wireOp",EDGE,"E4.right"),sQuery(id+"F0.wireOp",EDGE,"E5.trimOffspring"),sQuery(id+"F0.wireOp",EDGE,"E6.trimOffspring"),sQuery(id+"F0.wireOp",EDGE,"E7.trimOffspring"),sQuery(id+"F0.wireOp",EDGE,"E8"),sQuery(id+"F0.wireOp",EDGE,"E9.bottom"),sQuery(id+"F0.wireOp",EDGE,"E9.top"),sQuery(id+"F0.wireOp",EDGE,"E9.left"),sQuery(id+"F0.wireOp",EDGE,"E9.right"),sQuery(id+"F0.wireOp",EDGE,"E10.bottom"),sQuery(id+"F0.wireOp",EDGE,"E10.top"),sQuery(id+"F0.wireOp",EDGE,"E10.left"),sQuery(id+"F0.wireOp",EDGE,"E10.right"),sQuery(id+"F0.wireOp",EDGE,"E11.trimOffspring"),sQuery(id+"F0.wireOp",EDGE,"E12.trimOffspring"),sQuery(id+"F0.wireOp",EDGE,"E13.trimOffspring"),sQuery(id+"F0.wireOp",EDGE,"E14.trimOffspring"),sQuery(id+"F0.wireOp",EDGE,"E15.trimOffspring"),sQuery(id+"F0.wireOp",EDGE,"E16.trimOffspring"),sQuery(id+"F0.wireOp",EDGE,"E17.trimOffspring"),sQuery(id+"F0.wireOp",EDGE,"E18.trimOffspring"),sQuery(id+"F0.wireOp",EDGE,"E19.1.0"),sQuery(id+"F0.wireOp",EDGE,"E19.1.1"),sQuery(id+"F0.wireOp",EDGE,"E19.1.2"),sQuery(id+"F0.wireOp",EDGE,"E19.1.3"),sQuery(id+"F0.wireOp",EDGE,"E19.1.4"),sQuery(id+"F0.wireOp",EDGE,"E19.1.5"),sQuery(id+"F0.wireOp",EDGE,"E19.1.6"),sQuery(id+"F0.wireOp",EDGE,"E19.1.7"),sQuery(id+"F0.wireOp",EDGE,"E19.1.8"),sQuery(id+"F0.wireOp",EDGE,"E19.1.9"),sQuery(id+"F0.wireOp",EDGE,"E19.1.10"),sQuery(id+"F0.wireOp",EDGE,"E19.1.11"),sQuery(id+"F0.wireOp",EDGE,"E19.1.12"),sQuery(id+"F0.wireOp",EDGE,"E19.1.13"),sQuery(id+"F0.wireOp",EDGE,"E19.1.14"),sQuery(id+"F0.wireOp",EDGE,"E19.1.15"),sQuery(id+"F0.wireOp",EDGE,"E19.1.16"),sQuery(id+"F0.wireOp",EDGE,"E19.1.17"),sQuery(id+"F0.wireOp",EDGE,"E19.1.18"),sQuery(id+"F0.wireOp",EDGE,"E19.1.19"),sQuery(id+"F0.wireOp",EDGE,"E19.1.20"),sQuery(id+"F0.wireOp",EDGE,"E19.1.21"),sQuery(id+"F0.wireOp",EDGE,"E19.1.22"),sQuery(id+"F0.wireOp",EDGE,"E19.1.23"),sQuery(id+"F0.wireOp",EDGE,"E19.1.24"),sQuery(id+"F0.wireOp",EDGE,"E19.1.25"),sQuery(id+"F0.wireOp",EDGE,"E19.1.26"),sQuery(id+"F0.wireOp",EDGE,"E19.1.27"),sQuery(id+"F0.wireOp",EDGE,"E19.1.28"),sQuery(id+"F0.wireOp",EDGE,"E19.1.29"),sQuery(id+"F0.wireOp",EDGE,"E19.1.30"),sQuery(id+"F0.wireOp",EDGE,"E19.2.0"),sQuery(id+"F0.wireOp",EDGE,"E19.2.1"),sQuery(id+"F0.wireOp",EDGE,"E19.2.2"),sQuery(id+"F0.wireOp",EDGE,"E19.2.3"),sQuery(id+"F0.wireOp",EDGE,"E19.2.4"),sQuery(id+"F0.wireOp",EDGE,"E19.2.5"),sQuery(id+"F0.wireOp",EDGE,"E19.2.6"),sQuery(id+"F0.wireOp",EDGE,"E19.2.7"),sQuery(id+"F0.wireOp",EDGE,"E19.2.8"),sQuery(id+"F0.wireOp",EDGE,"E19.2.9"),sQuery(id+"F0.wireOp",EDGE,"E19.2.10"),sQuery(id+"F0.wireOp",EDGE,"E19.2.11"),sQuery(id+"F0.wireOp",EDGE,"E19.2.12"),sQuery(id+"F0.wireOp",EDGE,"E19.2.13"),sQuery(id+"F0.wireOp",EDGE,"E19.2.14"),sQuery(id+"F0.wireOp",EDGE,"E19.2.15"),sQuery(id+"F0.wireOp",EDGE,"E19.2.16"),sQuery(id+"F0.wireOp",EDGE,"E19.2.17"),sQuery(id+"F0.wireOp",EDGE,"E19.2.18"),sQuery(id+"F0.wireOp",EDGE,"E19.2.19"),sQuery(id+"F0.wireOp",EDGE,"E19.2.20"),sQuery(id+"F0.wireOp",EDGE,"E19.2.21"),sQuery(id+"F0.wireOp",EDGE,"E19.2.22"),sQuery(id+"F0.wireOp",EDGE,"E19.2.23"),sQuery(id+"F0.wireOp",EDGE,"E19.2.24"),sQuery(id+"F0.wireOp",EDGE,"E19.2.25"),sQuery(id+"F0.wireOp",EDGE,"E19.2.26"),sQuery(id+"F0.wireOp",EDGE,"E19.2.27"),sQuery(id+"F0.wireOp",EDGE,"E19.2.28"),sQuery(id+"F0.wireOp",EDGE,"E19.2.29"),sQuery(id+"F0.wireOp",EDGE,"E19.2.30"),sQuery(id+"F0.wireOp",EDGE,"E19.3.0"),sQuery(id+"F0.wireOp",EDGE,"E19.3.1"),sQuery(id+"F0.wireOp",EDGE,"E19.3.2"),sQuery(id+"F0.wireOp",EDGE,"E19.3.3"),sQuery(id+"F0.wireOp",EDGE,"E19.3.4"),sQuery(id+"F0.wireOp",EDGE,"E19.3.5"),sQuery(id+"F0.wireOp",EDGE,"E19.3.6"),sQuery(id+"F0.wireOp",EDGE,"E19.3.7"),sQuery(id+"F0.wireOp",EDGE,"E19.3.8"),sQuery(id+"F0.wireOp",EDGE,"E19.3.9"),sQuery(id+"F0.wireOp",EDGE,"E19.3.10"),sQuery(id+"F0.wireOp",EDGE,"E19.3.11"),sQuery(id+"F0.wireOp",EDGE,"E19.3.12"),sQuery(id+"F0.wireOp",EDGE,"E19.3.13"),sQuery(id+"F0.wireOp",EDGE,"E19.3.14"),sQuery(id+"F0.wireOp",EDGE,"E19.3.15"),sQuery(id+"F0.wireOp",EDGE,"E19.3.16"),sQuery(id+"F0.wireOp",EDGE,"E19.3.17"),sQuery(id+"F0.wireOp",EDGE,"E19.3.18"),sQuery(id+"F0.wireOp",EDGE,"E19.3.19"),sQuery(id+"F0.wireOp",EDGE,"E19.3.20"),sQuery(id+"F0.wireOp",EDGE,"E19.3.21"),sQuery(id+"F0.wireOp",EDGE,"E19.3.22"),sQuery(id+"F0.wireOp",EDGE,"E19.3.23"),sQuery(id+"F0.wireOp",EDGE,"E19.3.24"),sQuery(id+"F0.wireOp",EDGE,"E19.3.25"),sQuery(id+"F0.wireOp",EDGE,"E19.3.26"),sQuery(id+"F0.wireOp",EDGE,"E19.3.27"),sQuery(id+"F0.wireOp",EDGE,"E19.3.28"),sQuery(id+"F0.wireOp",EDGE,"E19.3.29"),sQuery(id+"F0.wireOp",EDGE,"E19.3.30"),sQuery(id+"F0.wireOp",EDGE,"E19.4.0"),sQuery(id+"F0.wireOp",EDGE,"E19.4.1"),sQuery(id+"F0.wireOp",EDGE,"E19.4.2"),sQuery(id+"F0.wireOp",EDGE,"E19.4.3"),sQuery(id+"F0.wireOp",EDGE,"E19.4.4"),sQuery(id+"F0.wireOp",EDGE,"E19.4.5"),sQuery(id+"F0.wireOp",EDGE,"E19.4.6"),sQuery(id+"F0.wireOp",EDGE,"E19.4.7"),sQuery(id+"F0.wireOp",EDGE,"E19.4.8"),sQuery(id+"F0.wireOp",EDGE,"E19.4.9"),sQuery(id+"F0.wireOp",EDGE,"E19.4.10"),sQuery(id+"F0.wireOp",EDGE,"E19.4.11"),sQuery(id+"F0.wireOp",EDGE,"E19.4.12"),sQuery(id+"F0.wireOp",EDGE,"E19.4.13"),sQuery(id+"F0.wireOp",EDGE,"E19.4.14"),sQuery(id+"F0.wireOp",EDGE,"E19.4.15"),sQuery(id+"F0.wireOp",EDGE,"E19.4.16"),sQuery(id+"F0.wireOp",EDGE,"E19.4.17"),sQuery(id+"F0.wireOp",EDGE,"E19.4.18"),sQuery(id+"F0.wireOp",EDGE,"E19.4.19"),sQuery(id+"F0.wireOp",EDGE,"E19.4.20"),sQuery(id+"F0.wireOp",EDGE,"E19.4.21"),sQuery(id+"F0.wireOp",EDGE,"E19.4.22"),sQuery(id+"F0.wireOp",EDGE,"E19.4.23"),sQuery(id+"F0.wireOp",EDGE,"E19.4.24"),sQuery(id+"F0.wireOp",EDGE,"E19.4.25"),sQuery(id+"F0.wireOp",EDGE,"E19.4.26"),sQuery(id+"F0.wireOp",EDGE,"E19.4.27"),sQuery(id+"F0.wireOp",EDGE,"E19.4.28"),sQuery(id+"F0.wireOp",EDGE,"E19.4.29"),sQuery(id+"F0.wireOp",EDGE,"E19.4.30"),sQuery(id+"F0.wireOp",EDGE,"E19.5.0"),sQuery(id+"F0.wireOp",EDGE,"E19.5.1"),sQuery(id+"F0.wireOp",EDGE,"E19.5.2"),sQuery(id+"F0.wireOp",EDGE,"E19.5.3"),sQuery(id+"F0.wireOp",EDGE,"E19.5.4"),sQuery(id+"F0.wireOp",EDGE,"E19.5.5"),sQuery(id+"F0.wireOp",EDGE,"E19.5.6"),sQuery(id+"F0.wireOp",EDGE,"E19.5.7"),sQuery(id+"F0.wireOp",EDGE,"E19.5.8"),sQuery(id+"F0.wireOp",EDGE,"E19.5.9"),sQuery(id+"F0.wireOp",EDGE,"E19.5.10"),sQuery(id+"F0.wireOp",EDGE,"E19.5.11"),sQuery(id+"F0.wireOp",EDGE,"E19.5.12"),sQuery(id+"F0.wireOp",EDGE,"E19.5.13"),sQuery(id+"F0.wireOp",EDGE,"E19.5.14"),sQuery(id+"F0.wireOp",EDGE,"E19.5.15"),sQuery(id+"F0.wireOp",EDGE,"E19.5.16"),sQuery(id+"F0.wireOp",EDGE,"E19.5.17"),sQuery(id+"F0.wireOp",EDGE,"E19.5.18"),sQuery(id+"F0.wireOp",EDGE,"E19.5.19"),sQuery(id+"F0.wireOp",EDGE,"E19.5.20"),sQuery(id+"F0.wireOp",EDGE,"E19.5.21"),sQuery(id+"F0.wireOp",EDGE,"E19.5.22"),sQuery(id+"F0.wireOp",EDGE,"E19.5.23"),sQuery(id+"F0.wireOp",EDGE,"E19.5.24"),sQuery(id+"F0.wireOp",EDGE,"E19.5.25"),sQuery(id+"F0.wireOp",EDGE,"E19.5.26"),sQuery(id+"F0.wireOp",EDGE,"E19.5.27"),sQuery(id+"F0.wireOp",EDGE,"E19.5.28"),sQuery(id+"F0.wireOp",EDGE,"E19.5.29"),sQuery(id+"F0.wireOp",EDGE,"E19.5.30"),sQuery(id+"F0.wireOp",EDGE,"E20.trimOffspring"),sQuery(id+"F0.wireOp",EDGE,"E21.trimOffspring"),sQuery(id+"F0.wireOp",EDGE,"E22.trimOffspring"),sQuery(id+"F0.wireOp",EDGE,"E23.trimOffspring"),sQuery(id+"F0.wireOp",EDGE,"E24.trimOffspring")])],"isStart":false});
            var sketch = newSketch(context, id + "F5", { "sketchPlane" : qUnion([Q0])});
            skArc(sketch, "E25.0", {"start": v(-1, 12.46) * mm, "mid": v(-6.25, 10.83) * mm, "end": v(-10.3, 7.1) * mm});
            skArc(sketch, "E26.0", {"start": v(-11.3, 5.36) * mm, "mid": v(-12.5, 0) * mm, "end": v(-11.3, -5.36) * mm});
            skArc(sketch, "E27.0", {"start": v(-10.3, -7.1) * mm, "mid": v(-6.25, -10.83) * mm, "end": v(-1, -12.46) * mm});
            skArc(sketch, "E28.0", {"start": v(1, -12.46) * mm, "mid": v(6.25, -10.83) * mm, "end": v(10.3, -7.1) * mm});
            skArc(sketch, "E29.0", {"start": v(11.3, -5.36) * mm, "mid": v(12.5, 0) * mm, "end": v(11.3, 5.36) * mm});
            skArc(sketch, "E30.0", {"start": v(10.3, 7.1) * mm, "mid": v(6.25, 10.83) * mm, "end": v(1, 12.46) * mm});
            skArc(sketch, "E31.0", {"start": v(9.86, 6.85) * mm, "mid": v(6, 10.4) * mm, "end": v(1, 11.96) * mm});
            skArc(sketch, "E32.0", {"start": v(10.86, -5.11) * mm, "mid": v(12, 0) * mm, "end": v(10.86, 5.11) * mm});
            skArc(sketch, "E33.0", {"start": v(1, -11.96) * mm, "mid": v(6, -10.4) * mm, "end": v(9.86, -6.85) * mm});
            skArc(sketch, "E34.0", {"start": v(-9.86, -6.85) * mm, "mid": v(-6, -10.4) * mm, "end": v(-1, -11.96) * mm});
            skArc(sketch, "E35.0", {"start": v(-10.86, 5.11) * mm, "mid": v(-12, 0) * mm, "end": v(-10.86, -5.11) * mm});
            skArc(sketch, "E36.0", {"start": v(-1, 11.96) * mm, "mid": v(-6, 10.4) * mm, "end": v(-9.86, 6.85) * mm});
            skLineSegment(sketch, "E37", {"start": v(-1, 12.46) * mm, "end": v(-1, 11.96) * mm});
            skLineSegment(sketch, "E38", {"start": v(1, 12.46) * mm, "end": v(1, 11.96) * mm});
            skLineSegment(sketch, "E39", {"start": v(-11.3, 5.36) * mm, "end": v(-10.86, 5.11) * mm});
            skLineSegment(sketch, "E40", {"start": v(-10.3, 7.1) * mm, "end": v(-9.86, 6.85) * mm});
            skLineSegment(sketch, "E41", {"start": v(-11.3, -5.36) * mm, "end": v(-10.86, -5.11) * mm});
            skLineSegment(sketch, "E42", {"start": v(-10.3, -7.1) * mm, "end": v(-9.86, -6.85) * mm});
            skLineSegment(sketch, "E43", {"start": v(-1, -11.96) * mm, "end": v(-1, -12.46) * mm});
            skLineSegment(sketch, "E44", {"start": v(1, -11.96) * mm, "end": v(1, -12.46) * mm});
            skLineSegment(sketch, "E45", {"start": v(9.86, -6.85) * mm, "end": v(10.3, -7.1) * mm});
            skLineSegment(sketch, "E46", {"start": v(10.86, -5.11) * mm, "end": v(11.3, -5.36) * mm});
            skLineSegment(sketch, "E47", {"start": v(9.86, 6.85) * mm, "end": v(10.3, 7.1) * mm});
            skLineSegment(sketch, "E48", {"start": v(10.86, 5.11) * mm, "end": v(11.3, 5.36) * mm});
            skSolve(sketch);
        }
        {
            var Q0;
            Q0=qSketchRegion(id+"F5",true);
            extrude(context, id + "F6", {"entities" : qUnion([Q0]), "operationType" : NewBodyOperationType.REMOVE, "endBound" : BoundingType.THROUGH_ALL, "oppositeDirection" : true, "depth" : 25 * mm, "offsetDistance" : 25 * mm});
        }
        {
            var Q0;
            Q0=makeQuery(id+"F1.opExtrude","SWEPT_EDGE",EDGE,{"disambiguationData":[OSD([sQuery(id+"F0.wireOp",EDGE,"E19.1.17"),sQuery(id+"F0.wireOp",EDGE,"E19.1.20")])]});
            var Q1;
            Q1=makeQuery(id+"F1.opExtrude","SWEPT_EDGE",EDGE,{"disambiguationData":[OSD([sQuery(id+"F0.wireOp",EDGE,"E19.1.21"),sQuery(id+"F0.wireOp",EDGE,"E19.1.26")])]});
            var Q2;
            Q2=makeQuery(id+"F1.opExtrude","SWEPT_EDGE",EDGE,{"disambiguationData":[OSD([sQuery(id+"F0.wireOp",EDGE,"E4.right"),sQuery(id+"F0.wireOp",EDGE,"E6.trimOffspring")])]});
            var Q3;
            Q3=makeQuery(id+"F1.opExtrude","SWEPT_EDGE",EDGE,{"disambiguationData":[OSD([sQuery(id+"F0.wireOp",EDGE,"E1.bottom"),sQuery(id+"F0.wireOp",EDGE,"E4.left")])]});
            var Q4;
            Q4=makeQuery(id+"F1.opExtrude","SWEPT_EDGE",EDGE,{"disambiguationData":[OSD([sQuery(id+"F0.wireOp",EDGE,"E19.5.17"),sQuery(id+"F0.wireOp",EDGE,"E19.5.20")])]});
            var Q5;
            Q5=makeQuery(id+"F1.opExtrude","SWEPT_EDGE",EDGE,{"disambiguationData":[OSD([sQuery(id+"F0.wireOp",EDGE,"E19.5.21"),sQuery(id+"F0.wireOp",EDGE,"E19.5.26")])]});
            var Q6;
            Q6=makeQuery(id+"F1.opExtrude","SWEPT_EDGE",EDGE,{"disambiguationData":[OSD([sQuery(id+"F0.wireOp",EDGE,"E19.4.17"),sQuery(id+"F0.wireOp",EDGE,"E19.4.20")])]});
            var Q7;
            Q7=makeQuery(id+"F1.opExtrude","SWEPT_EDGE",EDGE,{"disambiguationData":[OSD([sQuery(id+"F0.wireOp",EDGE,"E19.4.21"),sQuery(id+"F0.wireOp",EDGE,"E19.4.26")])]});
            var Q8;
            Q8=makeQuery(id+"F1.opExtrude","SWEPT_EDGE",EDGE,{"disambiguationData":[OSD([sQuery(id+"F0.wireOp",EDGE,"E19.3.17"),sQuery(id+"F0.wireOp",EDGE,"E19.3.20")])]});
            var Q9;
            Q9=makeQuery(id+"F1.opExtrude","SWEPT_EDGE",EDGE,{"disambiguationData":[OSD([sQuery(id+"F0.wireOp",EDGE,"E19.3.21"),sQuery(id+"F0.wireOp",EDGE,"E19.3.26")])]});
            var Q10;
            Q10=makeQuery(id+"F1.opExtrude","SWEPT_EDGE",EDGE,{"disambiguationData":[OSD([sQuery(id+"F0.wireOp",EDGE,"E19.2.17"),sQuery(id+"F0.wireOp",EDGE,"E19.2.20")])]});
            var Q11;
            Q11=makeQuery(id+"F1.opExtrude","SWEPT_EDGE",EDGE,{"disambiguationData":[OSD([sQuery(id+"F0.wireOp",EDGE,"E19.2.21"),sQuery(id+"F0.wireOp",EDGE,"E19.2.26")])]});
            var Q12;
            Q12=makeQuery(id+"F6.boolean.opBoolean","COPY",EDGE,{"derivedFrom":makeQuery(id+"F6.opExtrude","SWEPT_EDGE",EDGE,{"disambiguationData":[OSD([sQuery(id+"F5.wireOp",EDGE,"E34.0"),sQuery(id+"F5.wireOp",EDGE,"E42")])]})});
            var Q13;
            Q13=makeQuery(id+"F6.boolean.opBoolean","COPY",EDGE,{"derivedFrom":makeQuery(id+"F6.opExtrude","SWEPT_EDGE",EDGE,{"disambiguationData":[OSD([sQuery(id+"F5.wireOp",EDGE,"E35.0"),sQuery(id+"F5.wireOp",EDGE,"E41")])]})});
            var Q14;
            Q14=makeQuery(id+"F6.boolean.opBoolean","COPY",EDGE,{"derivedFrom":makeQuery(id+"F6.opExtrude","SWEPT_EDGE",EDGE,{"disambiguationData":[OSD([sQuery(id+"F5.wireOp",EDGE,"E35.0"),sQuery(id+"F5.wireOp",EDGE,"E39")])]})});
            var Q15;
            Q15=makeQuery(id+"F6.boolean.opBoolean","COPY",EDGE,{"derivedFrom":makeQuery(id+"F6.opExtrude","SWEPT_EDGE",EDGE,{"disambiguationData":[OSD([sQuery(id+"F5.wireOp",EDGE,"E36.0"),sQuery(id+"F5.wireOp",EDGE,"E40")])]})});
            var Q16;
            Q16=makeQuery(id+"F6.boolean.opBoolean","COPY",EDGE,{"derivedFrom":makeQuery(id+"F6.opExtrude","SWEPT_EDGE",EDGE,{"disambiguationData":[OSD([sQuery(id+"F5.wireOp",EDGE,"E36.0"),sQuery(id+"F5.wireOp",EDGE,"E37")])]})});
            var Q17;
            Q17=makeQuery(id+"F6.boolean.opBoolean","COPY",EDGE,{"derivedFrom":makeQuery(id+"F6.opExtrude","SWEPT_EDGE",EDGE,{"disambiguationData":[OSD([sQuery(id+"F5.wireOp",EDGE,"E31.0"),sQuery(id+"F5.wireOp",EDGE,"E38")])]})});
            var Q18;
            Q18=makeQuery(id+"F6.boolean.opBoolean","COPY",EDGE,{"derivedFrom":makeQuery(id+"F6.opExtrude","SWEPT_EDGE",EDGE,{"disambiguationData":[OSD([sQuery(id+"F5.wireOp",EDGE,"E31.0"),sQuery(id+"F5.wireOp",EDGE,"E47")])]})});
            var Q19;
            Q19=makeQuery(id+"F6.boolean.opBoolean","COPY",EDGE,{"derivedFrom":makeQuery(id+"F6.opExtrude","SWEPT_EDGE",EDGE,{"disambiguationData":[OSD([sQuery(id+"F5.wireOp",EDGE,"E32.0"),sQuery(id+"F5.wireOp",EDGE,"E48")])]})});
            var Q20;
            Q20=makeQuery(id+"F6.boolean.opBoolean","COPY",EDGE,{"derivedFrom":makeQuery(id+"F6.opExtrude","SWEPT_EDGE",EDGE,{"disambiguationData":[OSD([sQuery(id+"F5.wireOp",EDGE,"E32.0"),sQuery(id+"F5.wireOp",EDGE,"E46")])]})});
            var Q21;
            Q21=makeQuery(id+"F6.boolean.opBoolean","COPY",EDGE,{"derivedFrom":makeQuery(id+"F6.opExtrude","SWEPT_EDGE",EDGE,{"disambiguationData":[OSD([sQuery(id+"F5.wireOp",EDGE,"E33.0"),sQuery(id+"F5.wireOp",EDGE,"E45")])]})});
            var Q22;
            Q22=makeQuery(id+"F6.boolean.opBoolean","COPY",EDGE,{"derivedFrom":makeQuery(id+"F6.opExtrude","SWEPT_EDGE",EDGE,{"disambiguationData":[OSD([sQuery(id+"F5.wireOp",EDGE,"E33.0"),sQuery(id+"F5.wireOp",EDGE,"E44")])]})});
            var Q23;
            Q23=makeQuery(id+"F6.boolean.opBoolean","COPY",EDGE,{"derivedFrom":makeQuery(id+"F6.opExtrude","SWEPT_EDGE",EDGE,{"disambiguationData":[OSD([sQuery(id+"F5.wireOp",EDGE,"E34.0"),sQuery(id+"F5.wireOp",EDGE,"E43")])]})});
            fillet(context, id + "F7", {"entities" : qUnion([Q0, Q1, Q2, Q3, Q4, Q5, Q6, Q7, Q8, Q9, Q10, Q11, Q12, Q13, Q14, Q15, Q16, Q17, Q18, Q19, Q20, Q21, Q22, Q23]), "tangentPropagation" : true, "radius" : 0.5 * mm, "defaultsChanged" : false, "vertexSettings" : [], "allowEdgeOverflow" : false});
        }
        {
            var Q0;
            Q0=makeQuery(id+"F1.opExtrude","SWEPT_EDGE",EDGE,{"disambiguationData":[OSD([sQuery(id+"F0.wireOp",EDGE,"E19.1.3"),sQuery(id+"F0.wireOp",EDGE,"E19.1.9")])]});
            var Q1;
            Q1=makeQuery(id+"F1.opExtrude","SWEPT_EDGE",EDGE,{"disambiguationData":[OSD([sQuery(id+"F0.wireOp",EDGE,"E19.1.0"),sQuery(id+"F0.wireOp",EDGE,"E19.1.12")])]});
            var Q2;
            Q2=makeQuery(id+"F1.opExtrude","SWEPT_EDGE",EDGE,{"disambiguationData":[OSD([sQuery(id+"F0.wireOp",EDGE,"E19.2.0"),sQuery(id+"F0.wireOp",EDGE,"E19.2.12")])]});
            var Q3;
            Q3=makeQuery(id+"F1.opExtrude","SWEPT_EDGE",EDGE,{"disambiguationData":[OSD([sQuery(id+"F0.wireOp",EDGE,"E19.2.3"),sQuery(id+"F0.wireOp",EDGE,"E19.2.9")])]});
            var Q4;
            Q4=makeQuery(id+"F1.opExtrude","SWEPT_EDGE",EDGE,{"disambiguationData":[OSD([sQuery(id+"F0.wireOp",EDGE,"E19.3.0"),sQuery(id+"F0.wireOp",EDGE,"E19.3.12")])]});
            var Q5;
            Q5=makeQuery(id+"F1.opExtrude","SWEPT_EDGE",EDGE,{"disambiguationData":[OSD([sQuery(id+"F0.wireOp",EDGE,"E19.3.3"),sQuery(id+"F0.wireOp",EDGE,"E19.3.9")])]});
            var Q6;
            Q6=makeQuery(id+"F1.opExtrude","SWEPT_EDGE",EDGE,{"disambiguationData":[OSD([sQuery(id+"F0.wireOp",EDGE,"E19.4.0"),sQuery(id+"F0.wireOp",EDGE,"E19.4.12")])]});
            var Q7;
            Q7=makeQuery(id+"F1.opExtrude","SWEPT_EDGE",EDGE,{"disambiguationData":[OSD([sQuery(id+"F0.wireOp",EDGE,"E19.4.3"),sQuery(id+"F0.wireOp",EDGE,"E19.4.9")])]});
            var Q8;
            Q8=makeQuery(id+"F1.opExtrude","SWEPT_EDGE",EDGE,{"disambiguationData":[OSD([sQuery(id+"F0.wireOp",EDGE,"E19.5.0"),sQuery(id+"F0.wireOp",EDGE,"E19.5.12")])]});
            var Q9;
            Q9=makeQuery(id+"F1.opExtrude","SWEPT_EDGE",EDGE,{"disambiguationData":[OSD([sQuery(id+"F0.wireOp",EDGE,"E19.5.3"),sQuery(id+"F0.wireOp",EDGE,"E19.5.9")])]});
            var Q10;
            Q10=makeQuery(id+"F1.opExtrude","SWEPT_EDGE",EDGE,{"disambiguationData":[OSD([sQuery(id+"F0.wireOp",EDGE,"E0.bottom"),sQuery(id+"F0.wireOp",EDGE,"E0.left")])]});
            var Q11;
            Q11=makeQuery(id+"F1.opExtrude","SWEPT_EDGE",EDGE,{"disambiguationData":[OSD([sQuery(id+"F0.wireOp",EDGE,"E0.right"),sQuery(id+"F0.wireOp",EDGE,"E5.trimOffspring")])]});
            fillet(context, id + "F8", {"entities" : qUnion([Q0, Q1, Q2, Q3, Q4, Q5, Q6, Q7, Q8, Q9, Q10, Q11]), "tangentPropagation" : true, "radius" : 1.5 * mm, "defaultsChanged" : false, "vertexSettings" : [], "allowEdgeOverflow" : false});
        }
    });
